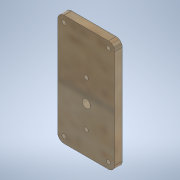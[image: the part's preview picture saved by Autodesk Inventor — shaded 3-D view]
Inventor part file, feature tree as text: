
AUTODESK INVENTOR PART (.ipt)
format: ipt  version: 2020.3 (Build 243373000, 373)  size: 147,456 bytes
history: native  units: mm
features: sketch x4, hole x3, other x1, extrude x1, fillet x1
ambient origin geometry x8: Origin, YZ Plane, XZ Plane, XY Plane, X Axis, Y Axis, Z Axis, Center Point
bodies: Body1 (feature_tree)
feature tree (10):
  other  "ソリッド1"
  extrude  "押し出し1"  Depth=41.0mm
  hole  "穴1"  [1 undecoded]
  fillet  "フィレット1"  Radius=4.5mm
  hole  "穴2"  [1 undecoded]
  hole  "穴3"  [1 undecoded]
  sketch  "スケッチ1"
  sketch  "スケッチ2"
  sketch  "スケッチ3"
  sketch  "スケッチ4"
note: 3 required parameter values undecoded (feature->parameter linkage not recoverable at this tier; creation-order binding heuristic only, values carry confidence <= 0.55)
